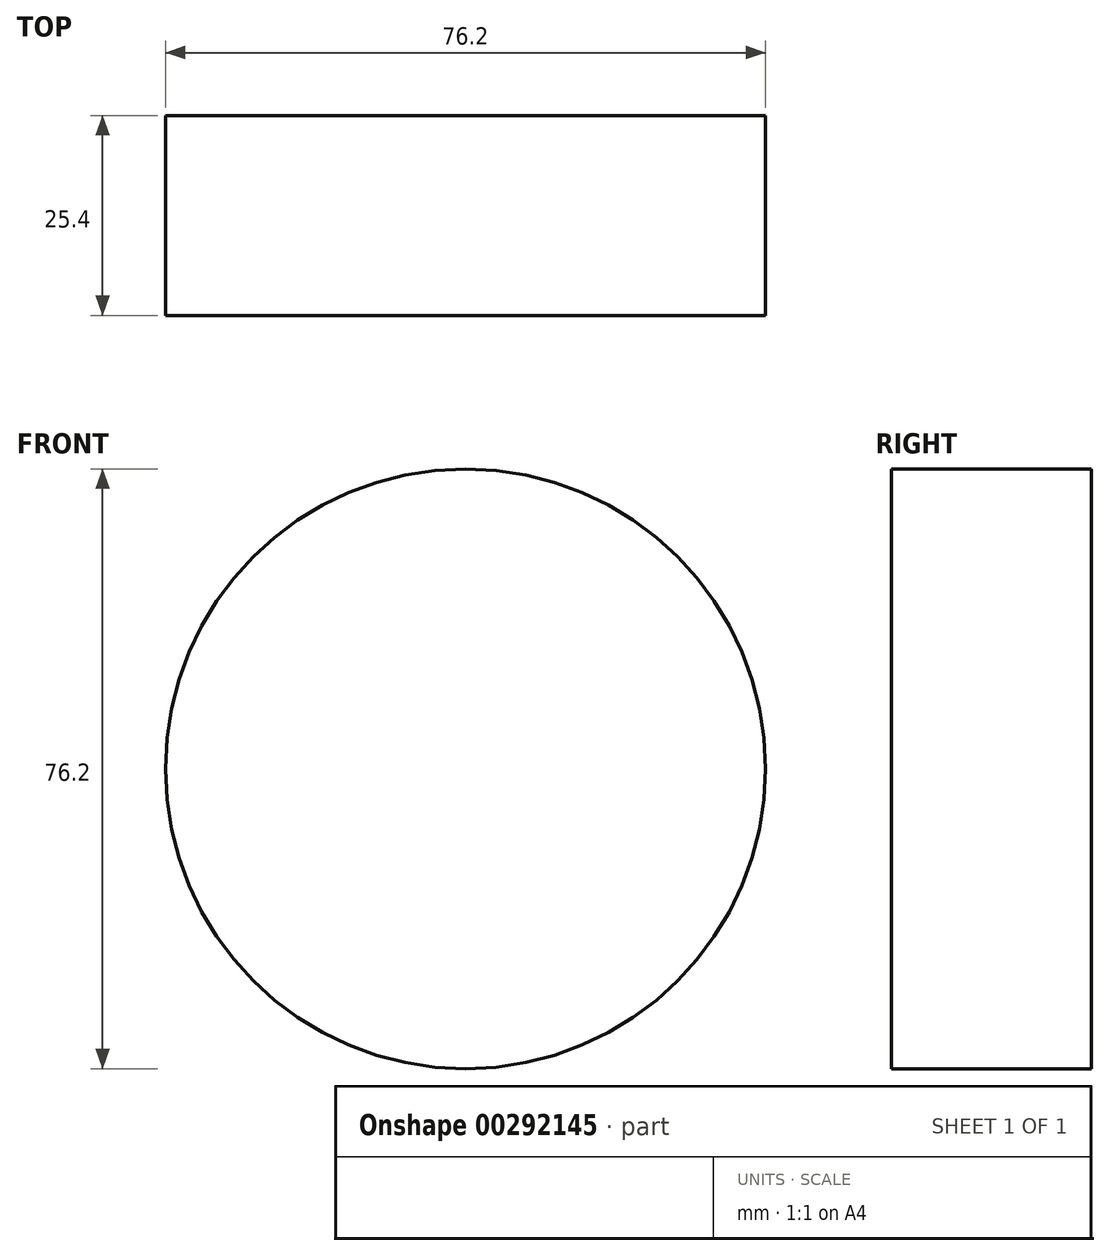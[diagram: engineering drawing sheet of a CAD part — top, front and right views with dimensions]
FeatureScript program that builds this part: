
annotation { "Feature Type Name" : "Feature", "Feature Type Description" : "" }
export const myFeature = defineFeature(function(context is Context, id is Id, definition is map)
    precondition{}
    {
        {
            var Q0;
            Q0=qCreatedBy(makeId("Front.planeOp"),FACE);
            var sketch = newSketch(context, id + "F0", { "sketchPlane" : qUnion([Q0])});
            skCircle(sketch, "E0", {"center": v(-12.6, 37.43) * mm, "radius": 38.1 * mm});
            skSolve(sketch);
        }
        {
            var Q0;
            Q0=makeQuery(id+"F0.imprint","IMPRINT",FACE,{"disambiguationData":[TD([[makeQuery(id+"F0.imprint","IMPRINT",EDGE,{"derivedFrom":sQuery(id+"F0.wireOp",EDGE,"E0")}),1.0]])]});
            extrude(context, id + "F1", {"entities" : qUnion([Q0]), "depth" : 25.4 * mm});
        }
        {
            var Q0;
            Q0=makeQuery(id+"F1.opExtrude","CAP_FACE",FACE,{"disambiguationData":[OSD([sQuery(id+"F0.wireOp",EDGE,"E0")])],"isStart":false});
            var sketch = newSketch(context, id + "F2", { "sketchPlane" : qUnion([Q0])});
            skArc(sketch, "E1", {"start": v(17.39, 60.93) * mm, "mid": v(6.36, 35.28) * mm, "end": v(11.37, 7.81) * mm});
            skSolve(sketch);
        }
    });
